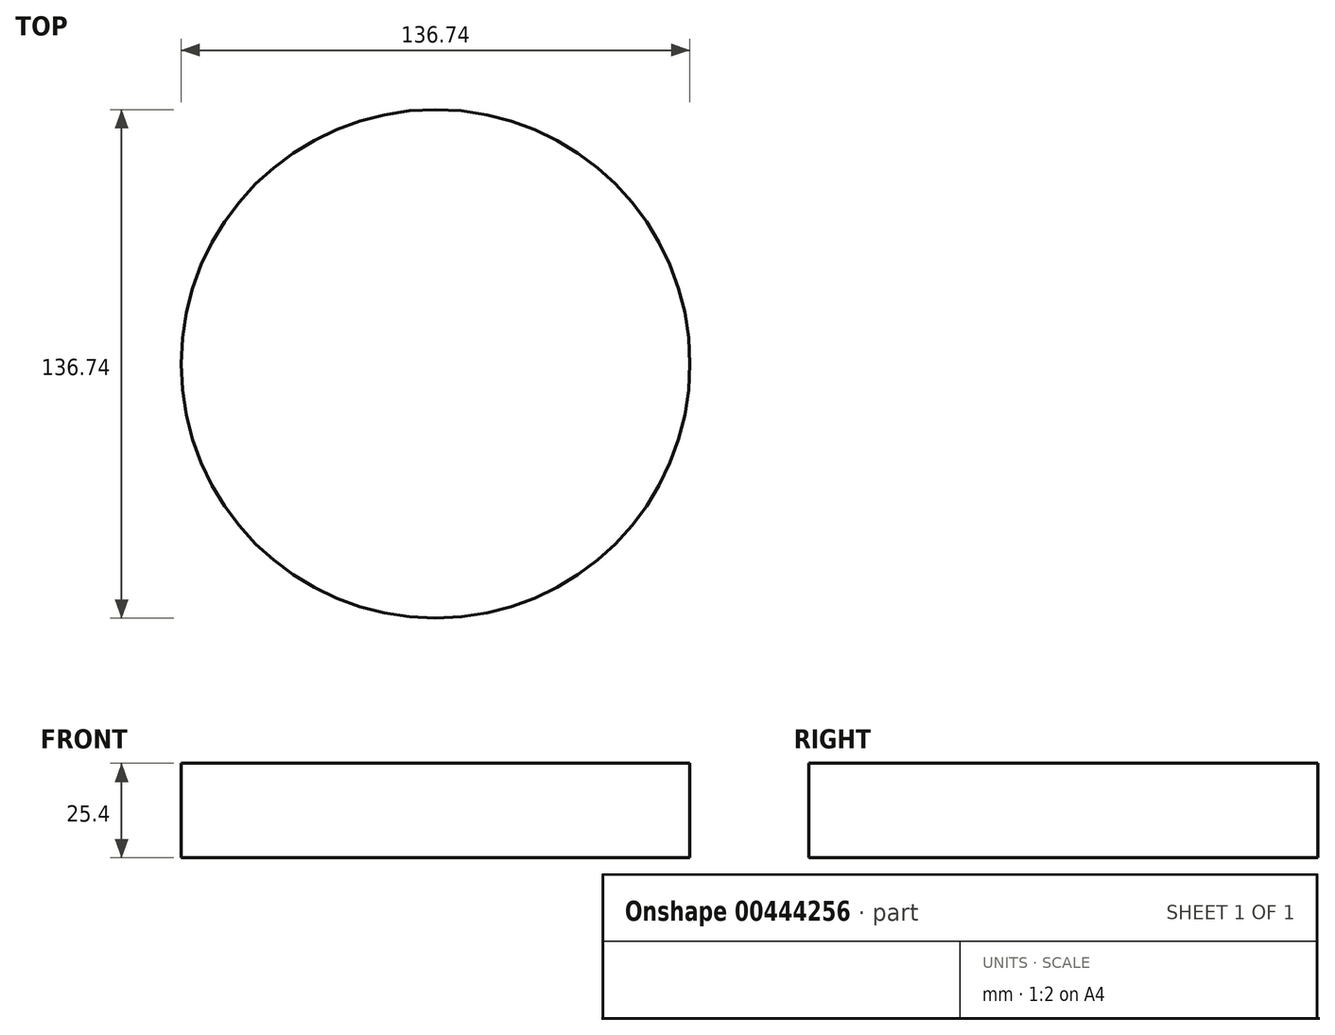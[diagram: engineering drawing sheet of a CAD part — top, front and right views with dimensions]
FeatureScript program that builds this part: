
annotation { "Feature Type Name" : "Feature", "Feature Type Description" : "" }
export const myFeature = defineFeature(function(context is Context, id is Id, definition is map)
    precondition{}
    {
        {
            var Q0;
            Q0=qCreatedBy(makeId("Top.planeOp"),FACE);
            var sketch = newSketch(context, id + "F0", { "sketchPlane" : qUnion([Q0])});
            skCircle(sketch, "E0", {"center": v(0, 0) * mm, "radius": 68.37 * mm});
            skSolve(sketch);
        }
        {
            var Q0;
            Q0 = qSketchRegion(id + "F0", true);
            extrude(context, id + "F1", {"entities" : qUnion([Q0]), "depth" : 25.4 * mm});
        }
    });
